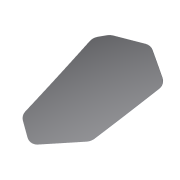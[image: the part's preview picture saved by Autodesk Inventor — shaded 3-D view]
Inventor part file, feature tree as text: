
AUTODESK INVENTOR PART (.ipt)
format: ipt  version: 2020 (Build 240168000, 168)  size: 226,816 bytes
history: native  units: mm
features: other x6, fillet x2, imported_body x1, extrude x1, mirror x1
ambient origin geometry x8: Origin, YZ Plane, XZ Plane, XY Plane, X Axis, Y Axis, Z Axis, Center Point
bodies: Solid1 (feature_tree)
feature tree (11):
  imported_body  "Base"
  extrude  "BaseFeature"  Depth=25.481807mm
  fillet  "SmallFilletsFeature"  Radius=18.849556mm
  fillet  "LargeFilletsFeature"  Radius=21.642083mm
  other  "SlopeProfileMiddlePlane"
  other  "SlopeProfileIntersect"
  other  "SlopeProfileIntersectFeature"
  other  "SlopeProfileSubtractFeature"
  mirror  "RightMirror"
  other  "SlopeProfilePlane"
  other  "SlopeProfileSubtract"
